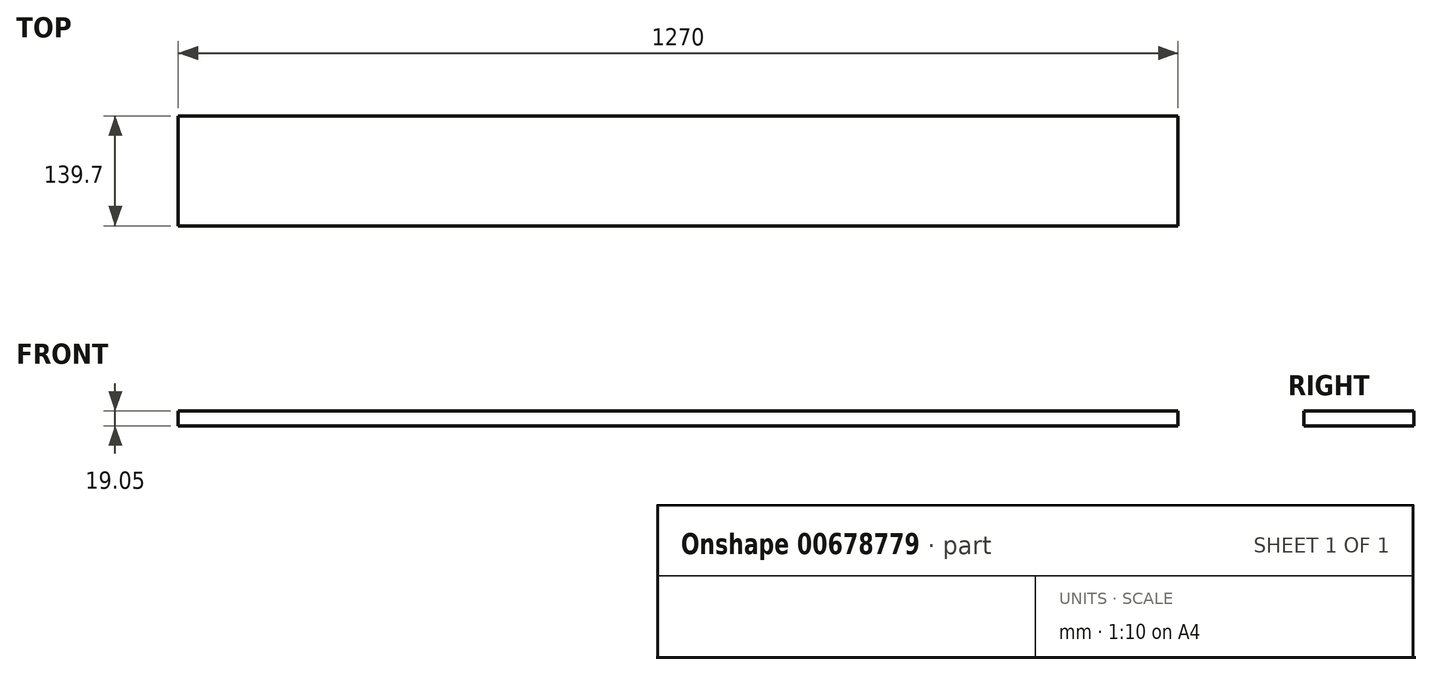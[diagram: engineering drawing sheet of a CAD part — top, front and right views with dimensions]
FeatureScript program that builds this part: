
annotation { "Feature Type Name" : "Feature", "Feature Type Description" : "" }
export const myFeature = defineFeature(function(context is Context, id is Id, definition is map)
    precondition{}
    {
        {
            var Q0;
            Q0=qCreatedBy(makeId("Top.planeOp"),FACE);
            var sketch = newSketch(context, id + "F0", { "sketchPlane" : qUnion([Q0])});
            skLineSegment(sketch, "E0.bottom", {"start": v(-223.5, 99.1) * mm, "end": v(1046.5, 99.1) * mm});
            skLineSegment(sketch, "E0.top", {"start": v(-223.5, -40.6) * mm, "end": v(1046.5, -40.6) * mm});
            skLineSegment(sketch, "E0.left", {"start": v(-223.5, 99.1) * mm, "end": v(-223.5, -40.6) * mm});
            skLineSegment(sketch, "E0.right", {"start": v(1046.5, 99.1) * mm, "end": v(1046.5, -40.6) * mm});
            skSolve(sketch);
        }
        {
            var Q0;
            Q0=makeQuery(id+"F0.imprint","IMPRINT",FACE,{"disambiguationData":[TD([[makeQuery(id+"F0.imprint","IMPRINT",EDGE,{"derivedFrom":sQuery(id+"F0.wireOp",EDGE,"E0.bottom")}),-1.0]])]});
            extrude(context, id + "F1", {"entities" : qUnion([Q0]), "depth" : 19.05 * mm, "offsetDistance" : 25.4 * mm});
        }
    });
